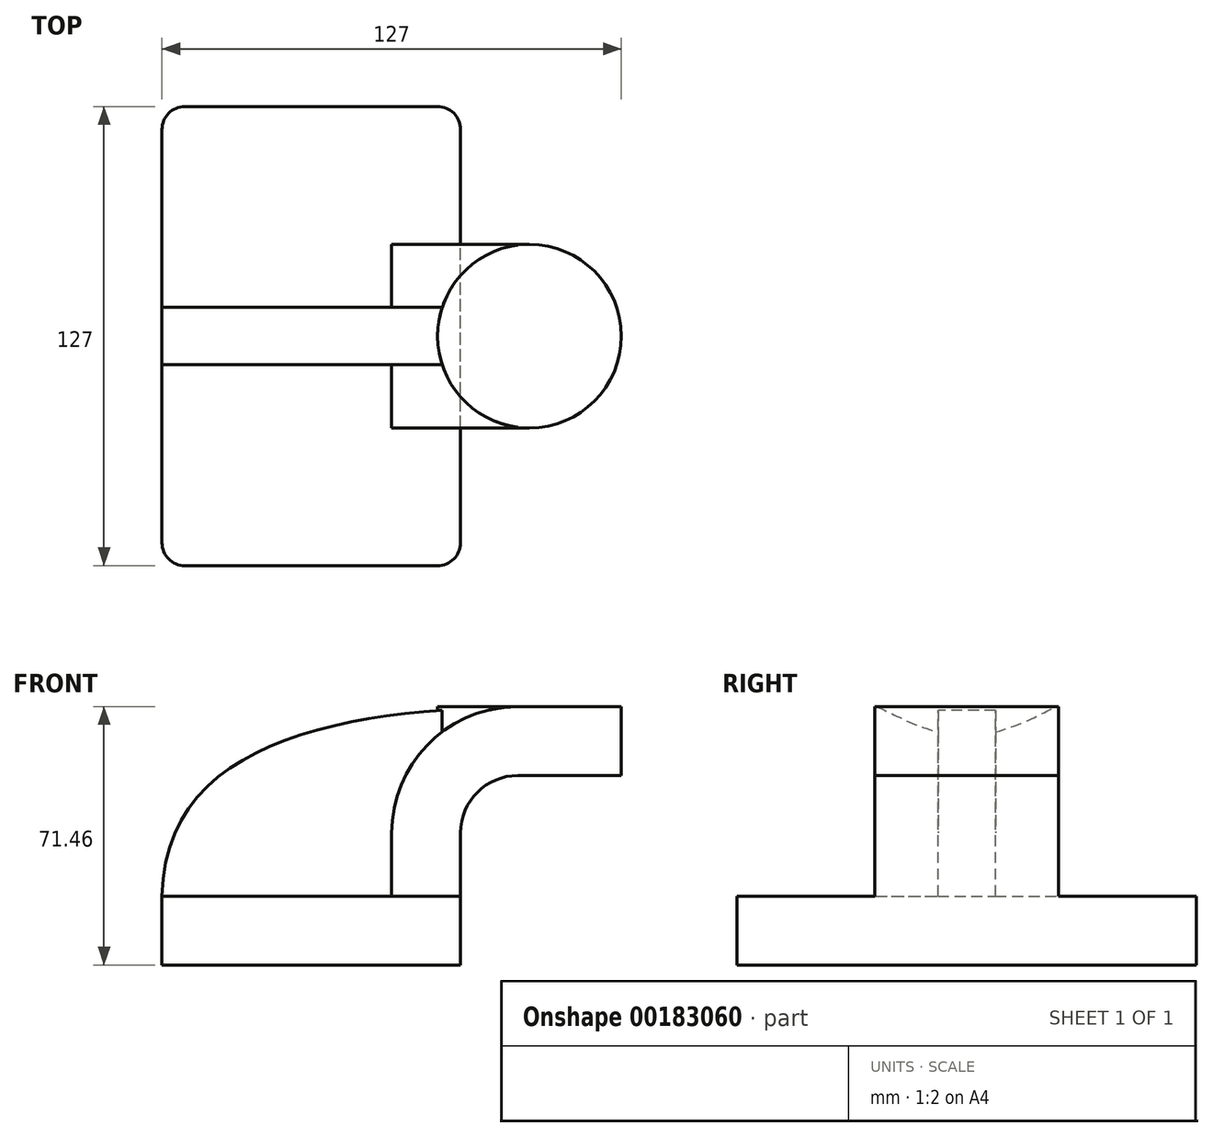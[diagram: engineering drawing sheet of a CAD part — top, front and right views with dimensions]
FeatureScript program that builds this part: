
annotation { "Feature Type Name" : "Feature", "Feature Type Description" : "" }
export const myFeature = defineFeature(function(context is Context, id is Id, definition is map)
    precondition{}
    {
        {
            var Q0;
            Q0=qCreatedBy(makeId("Front.planeOp"),FACE);
            var sketch = newSketch(context, id + "F0", { "sketchPlane" : qUnion([Q0])});
            skLineSegment(sketch, "E0.bottom", {"start": v(-41.28, -9.53) * mm, "end": v(41.28, -9.53) * mm});
            skLineSegment(sketch, "E0.top", {"start": v(-41.28, 9.52) * mm, "end": v(41.27, 9.52) * mm});
            skLineSegment(sketch, "E0.left", {"start": v(-41.27, -9.53) * mm, "end": v(-41.28, 9.52) * mm});
            skLineSegment(sketch, "E0.right", {"start": v(41.28, -9.53) * mm, "end": v(41.27, 9.52) * mm});
            skPoint(sketch, "E0.middle", {"position": v(0, 0) * mm});
            skLineSegment(sketch, "E1.bottom", {"start": v(60.33, 38.1) * mm, "end": v(111.13, 38.1) * mm});
            skLineSegment(sketch, "E1.top", {"start": v(60.33, 66.67) * mm, "end": v(111.13, 66.67) * mm});
            skLineSegment(sketch, "E1.left", {"start": v(60.33, 38.1) * mm, "end": v(60.33, 66.67) * mm});
            skLineSegment(sketch, "E1.right", {"start": v(111.13, 38.1) * mm, "end": v(111.13, 66.67) * mm});
            skPoint(sketch, "E1.middle", {"position": v(85.73, 52.39) * mm});
            skLineSegment(sketch, "E2", {"start": v(41.27, 9.52) * mm, "end": v(41.27, 27) * mm});
            skArc(sketch, "E3", {"start": v(41.27, 27) * mm, "mid": v(45.92, 38.23) * mm, "end": v(57.15, 42.88) * mm});
            skLineSegment(sketch, "E4", {"start": v(57.15, 42.88) * mm, "end": v(85.73, 42.88) * mm});
            skLineSegment(sketch, "E5.0", {"start": v(57.15, 61.93) * mm, "end": v(85.73, 61.93) * mm});
            skArc(sketch, "E5.1", {"start": v(22.22, 27) * mm, "mid": v(32.45, 51.7) * mm, "end": v(57.15, 61.93) * mm});
            skLineSegment(sketch, "E5.2", {"start": v(22.22, 9.52) * mm, "end": v(22.22, 27) * mm});
            skLineSegment(sketch, "E6", {"start": v(85.73, 38.1) * mm, "end": v(85.73, 66.67) * mm});
            skFitSpline(sketch, "E7", {"points": [v(-41.28, 9.53) * mm, v(57.15, 61.93) * mm], "startDerivative": vector(2.67, 132.04) * mm, "endDerivative": vector(140.33, 2.92) * mm});
            skSolve(sketch);
        }
        {
            var Q0;
            Q0=makeQuery(id+"F0.imprint","IMPRINT",FACE,{"disambiguationData":[TD([[makeQuery(id+"F0.imprint","IMPRINT",EDGE,{"derivedFrom":sQuery(id+"F0.wireOp",EDGE,"E0.bottom")}),1.0]])]});
            extrude(context, id + "F1", {"entities" : qUnion([Q0]), "endBound" : BoundingType.SYMMETRIC, "depth" : 127 * mm});
        }
        {
            var Q0;
            {var subQ1=sQuery(id+"F0.wireOp",EDGE,"E2");Q0=makeQuery(id+"F0.imprint","IMPRINT",FACE,{"disambiguationData":[TD([[makeQuery(id+"F0.imprint","IMPRINT",EDGE,{"derivedFrom":subQ1}),1.0]])]});}
            extrude(context, id + "F2", {"entities" : qUnion([Q0]), "operationType" : NewBodyOperationType.ADD, "endBound" : BoundingType.SYMMETRIC, "depth" : 50.8 * mm});
        }
        {
            var Q0;
            {var subQ3=sQuery(id+"F0.wireOp",EDGE,"E5.2");Q0=makeQuery(id+"F0.imprint","IMPRINT",FACE,{"disambiguationData":[TD([[makeQuery(id+"F0.imprint","IMPRINT",EDGE,{"derivedFrom":subQ3}),1.0]])]});}
            extrude(context, id + "F3", {"entities" : qUnion([Q0]), "operationType" : NewBodyOperationType.ADD, "endBound" : BoundingType.SYMMETRIC, "depth" : 15.88 * mm});
        }
        {
            var Q0;
            {var subQ0=sQuery(id+"F0.wireOp",EDGE,"E4");var subQ1=sQuery(id+"F0.wireOp",EDGE,"E1.left");var subQ2=makeQuery(id+"F0.imprint","INTERSECT",VERTEX,{"derivedFrom":[subQ1,subQ0]});Q0=makeQuery(id+"F0.imprint","IMPRINT",FACE,{"disambiguationData":[TD([[makeQuery(id+"F0.imprint","IMPRINT",EDGE,{"disambiguationData":[TD([[subQ2,-1.0]])],"derivedFrom":subQ1}),-1.0]])]});}
            var Q1;
            Q1=sQuery(id+"F0.wireOp",EDGE,"E1.left");
            revolve(context, id + "F4", {"operationType" : NewBodyOperationType.ADD, "entities" : qUnion([Q0]), "axis" : qUnion([Q1]), "revolveType" : RevolveType.FULL});
        }
        {
            var Q0;
            Q0=makeQuery(id+"F1.opExtrude","CAP_EDGE",EDGE,{"disambiguationData":[OSD([sQuery(id+"F0.wireOp",EDGE,"E0.left")])],"isStart":false});
            var Q1;
            Q1=makeQuery(id+"F1.opExtrude","CAP_EDGE",EDGE,{"disambiguationData":[OSD([sQuery(id+"F0.wireOp",EDGE,"E0.right")])],"isStart":false});
            var Q2;
            Q2=makeQuery(id+"F1.opExtrude","CAP_EDGE",EDGE,{"disambiguationData":[OSD([sQuery(id+"F0.wireOp",EDGE,"E0.right")])],"isStart":true});
            var Q3;
            Q3=makeQuery(id+"F1.opExtrude","CAP_EDGE",EDGE,{"disambiguationData":[OSD([sQuery(id+"F0.wireOp",EDGE,"E0.left")])],"isStart":true});
            fillet(context, id + "F5", {"entities" : qUnion([Q0, Q1, Q2, Q3]), "radius" : 6.35 * mm, "tangentPropagation" : true, "allowEdgeOverflow" : false});
        }
    });
